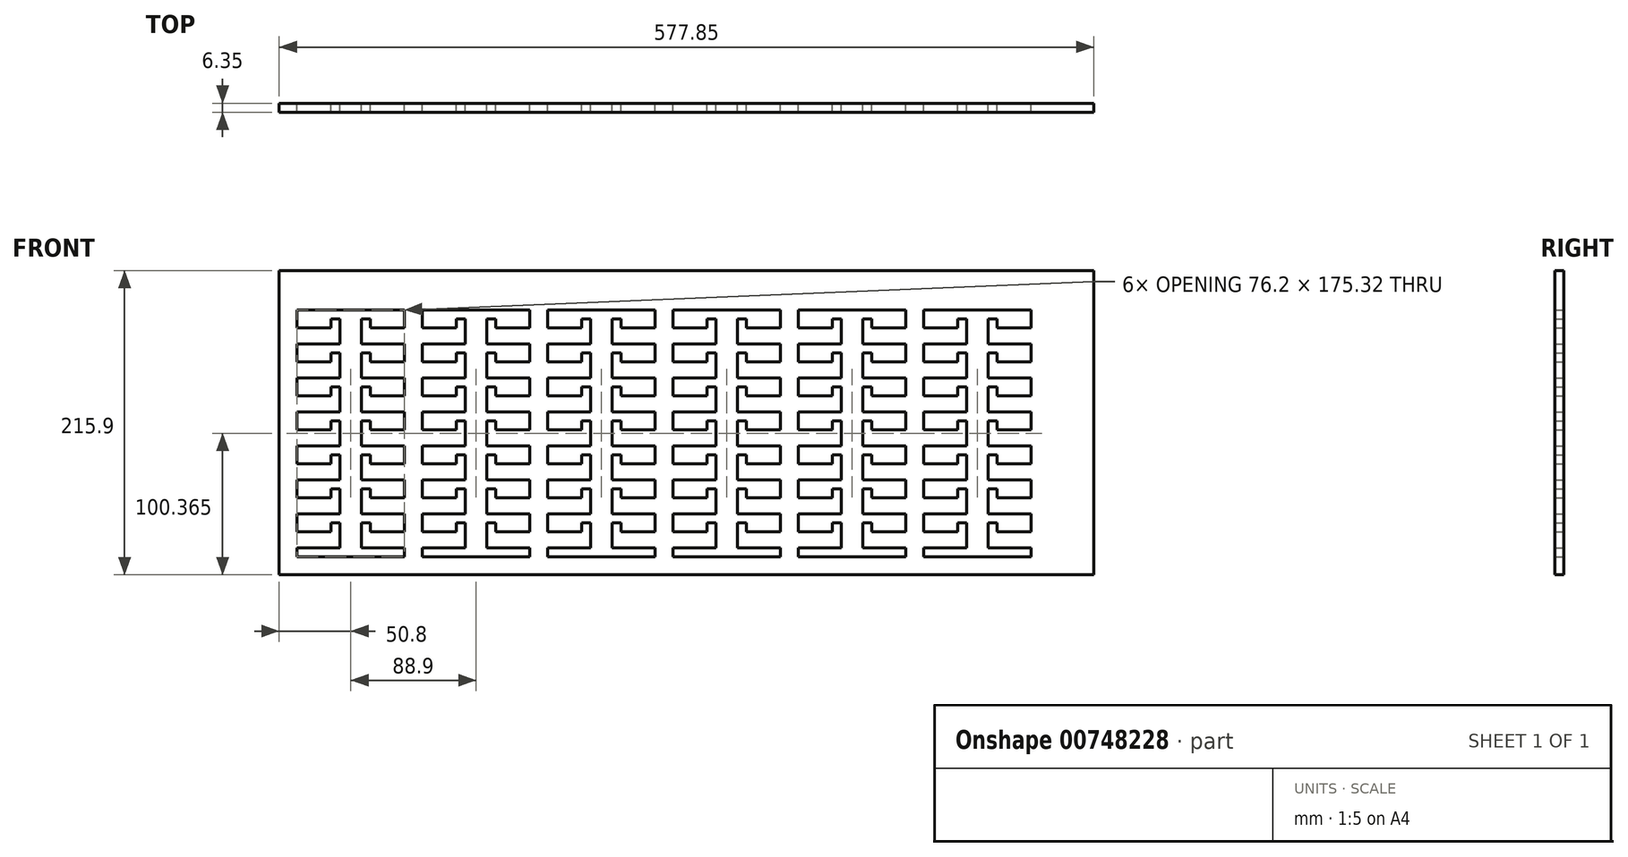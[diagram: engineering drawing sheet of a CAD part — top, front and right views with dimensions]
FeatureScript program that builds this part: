
annotation { "Feature Type Name" : "Feature", "Feature Type Description" : "" }
export const myFeature = defineFeature(function(context is Context, id is Id, definition is map)
    precondition{}
    {
        {
            var Q0;
            Q0=qCreatedBy(makeId("Front.planeOp"),FACE);
            var sketch = newSketch(context, id + "F0", { "sketchPlane" : qUnion([Q0])});
            skLineSegment(sketch, "E0", {"start": v(-97.96, -49.5) * mm, "end": v(-67.48, -49.5) * mm});
            skLineSegment(sketch, "E1", {"start": v(-67.48, -49.5) * mm, "end": v(-67.48, -31.72) * mm});
            skLineSegment(sketch, "E2", {"start": v(-67.48, -31.72) * mm, "end": v(-73.83, -31.72) * mm});
            skLineSegment(sketch, "E3", {"start": v(-73.83, -31.72) * mm, "end": v(-73.83, -38.07) * mm});
            skLineSegment(sketch, "E4", {"start": v(-73.83, -38.07) * mm, "end": v(-97.96, -38.07) * mm});
            skLineSegment(sketch, "E5", {"start": v(-97.96, -38.07) * mm, "end": v(-97.96, -25.37) * mm});
            skLineSegment(sketch, "E6", {"start": v(-97.96, -25.37) * mm, "end": v(-67.48, -25.37) * mm});
            skLineSegment(sketch, "E7", {"start": v(-67.48, -25.37) * mm, "end": v(-67.48, -7.6) * mm});
            skLineSegment(sketch, "E8", {"start": v(-67.48, -7.6) * mm, "end": v(-73.83, -7.6) * mm});
            skLineSegment(sketch, "E9", {"start": v(-73.83, -7.6) * mm, "end": v(-73.83, -13.94) * mm});
            skLineSegment(sketch, "E10", {"start": v(-73.83, -13.94) * mm, "end": v(-97.96, -13.94) * mm});
            skLineSegment(sketch, "E11", {"start": v(-97.96, -13.94) * mm, "end": v(-97.96, -1.24) * mm});
            skLineSegment(sketch, "E12", {"start": v(-97.96, -1.24) * mm, "end": v(-67.48, -1.24) * mm});
            skLineSegment(sketch, "E13", {"start": v(-67.48, -1.24) * mm, "end": v(-67.48, 16.54) * mm});
            skLineSegment(sketch, "E14", {"start": v(-67.48, 16.54) * mm, "end": v(-73.83, 16.54) * mm});
            skLineSegment(sketch, "E15", {"start": v(-73.83, 16.54) * mm, "end": v(-73.83, 10.19) * mm});
            skLineSegment(sketch, "E16", {"start": v(-73.83, 10.19) * mm, "end": v(-97.96, 10.19) * mm});
            skLineSegment(sketch, "E17", {"start": v(-97.96, 10.19) * mm, "end": v(-97.96, 22.89) * mm});
            skLineSegment(sketch, "E18", {"start": v(-97.96, 22.89) * mm, "end": v(-67.48, 22.89) * mm});
            skLineSegment(sketch, "E19", {"start": v(-67.48, 22.89) * mm, "end": v(-67.48, 40.67) * mm});
            skLineSegment(sketch, "E20", {"start": v(-67.48, 40.67) * mm, "end": v(-73.83, 40.67) * mm});
            skLineSegment(sketch, "E21", {"start": v(-73.83, 40.67) * mm, "end": v(-73.83, 34.32) * mm});
            skLineSegment(sketch, "E22", {"start": v(-73.83, 34.32) * mm, "end": v(-97.96, 34.32) * mm});
            skLineSegment(sketch, "E23", {"start": v(-97.96, 34.32) * mm, "end": v(-97.96, 47.02) * mm});
            skLineSegment(sketch, "E24", {"start": v(-21.76, -80.05) * mm, "end": v(-21.76, -73.63) * mm});
            skLineSegment(sketch, "E25", {"start": v(-21.76, -73.63) * mm, "end": v(-52.24, -73.63) * mm});
            skLineSegment(sketch, "E26", {"start": v(-52.24, -73.63) * mm, "end": v(-52.24, -55.85) * mm});
            skLineSegment(sketch, "E27", {"start": v(-52.24, -55.85) * mm, "end": v(-45.89, -55.85) * mm});
            skLineSegment(sketch, "E28", {"start": v(-45.89, -55.85) * mm, "end": v(-45.89, -62.2) * mm});
            skLineSegment(sketch, "E29", {"start": v(-45.89, -62.2) * mm, "end": v(-21.76, -62.2) * mm});
            skLineSegment(sketch, "E30", {"start": v(-21.76, -62.2) * mm, "end": v(-21.76, -49.5) * mm});
            skLineSegment(sketch, "E31", {"start": v(-21.76, -49.5) * mm, "end": v(-52.24, -49.5) * mm});
            skLineSegment(sketch, "E32", {"start": v(-52.24, -49.5) * mm, "end": v(-52.24, -31.72) * mm});
            skLineSegment(sketch, "E33", {"start": v(-52.24, -31.72) * mm, "end": v(-45.89, -31.72) * mm});
            skLineSegment(sketch, "E34", {"start": v(-45.89, -31.72) * mm, "end": v(-45.89, -38.07) * mm});
            skLineSegment(sketch, "E35", {"start": v(-45.89, -38.07) * mm, "end": v(-21.76, -38.07) * mm});
            skLineSegment(sketch, "E36", {"start": v(-21.76, -38.07) * mm, "end": v(-21.76, -25.37) * mm});
            skLineSegment(sketch, "E37", {"start": v(-21.76, -25.37) * mm, "end": v(-52.24, -25.37) * mm});
            skLineSegment(sketch, "E38", {"start": v(-52.24, -25.37) * mm, "end": v(-52.24, -7.6) * mm});
            skLineSegment(sketch, "E39", {"start": v(-52.24, -7.6) * mm, "end": v(-45.89, -7.6) * mm});
            skLineSegment(sketch, "E40", {"start": v(-45.89, -7.6) * mm, "end": v(-45.89, -13.94) * mm});
            skLineSegment(sketch, "E41", {"start": v(-45.89, -13.94) * mm, "end": v(-21.76, -13.94) * mm});
            skLineSegment(sketch, "E42", {"start": v(-21.76, -13.94) * mm, "end": v(-21.76, -1.24) * mm});
            skLineSegment(sketch, "E43", {"start": v(-21.76, -1.24) * mm, "end": v(-52.24, -1.24) * mm});
            skLineSegment(sketch, "E44", {"start": v(-52.24, -1.24) * mm, "end": v(-52.24, 16.54) * mm});
            skLineSegment(sketch, "E45", {"start": v(-52.24, 16.54) * mm, "end": v(-45.89, 16.54) * mm});
            skLineSegment(sketch, "E46", {"start": v(-45.89, 16.54) * mm, "end": v(-45.89, 10.19) * mm});
            skLineSegment(sketch, "E47", {"start": v(-45.89, 10.19) * mm, "end": v(-21.76, 10.19) * mm});
            skLineSegment(sketch, "E48", {"start": v(-21.76, 10.19) * mm, "end": v(-21.76, 22.89) * mm});
            skLineSegment(sketch, "E49", {"start": v(-21.76, 22.89) * mm, "end": v(-52.24, 22.89) * mm});
            skLineSegment(sketch, "E50", {"start": v(-52.24, 22.89) * mm, "end": v(-52.24, 40.67) * mm});
            skLineSegment(sketch, "E51", {"start": v(-52.24, 40.67) * mm, "end": v(-45.89, 40.67) * mm});
            skLineSegment(sketch, "E52", {"start": v(-45.89, 40.67) * mm, "end": v(-45.89, 34.32) * mm});
            skLineSegment(sketch, "E53", {"start": v(-45.89, 34.32) * mm, "end": v(-21.76, 34.32) * mm});
            skLineSegment(sketch, "E54", {"start": v(-21.76, 34.32) * mm, "end": v(-21.76, 47.02) * mm});
            skLineSegment(sketch, "E55", {"start": v(-67.48, -73.63) * mm, "end": v(-67.48, -55.85) * mm});
            skLineSegment(sketch, "E56", {"start": v(-73.83, -62.2) * mm, "end": v(-73.83, -55.85) * mm});
            skLineSegment(sketch, "E57", {"start": v(-73.83, -55.85) * mm, "end": v(-67.48, -55.85) * mm});
            skLineSegment(sketch, "E58", {"start": v(-67.48, -73.63) * mm, "end": v(-97.96, -73.63) * mm});
            skLineSegment(sketch, "E59", {"start": v(-97.96, -62.2) * mm, "end": v(-97.96, -49.5) * mm});
            skLineSegment(sketch, "E60", {"start": v(-97.96, -73.63) * mm, "end": v(-97.96, -80.05) * mm});
            skLineSegment(sketch, "E61", {"start": v(-97.96, -62.2) * mm, "end": v(-73.83, -62.2) * mm});
            skLineSegment(sketch, "E62", {"start": v(-97.96, -80.05) * mm, "end": v(-21.76, -80.05) * mm});
            skPoint(sketch, "E63", {"position": v(-59.86, -80.05) * mm});
            skLineSegment(sketch, "E64", {"start": v(-186.86, -49.5) * mm, "end": v(-156.38, -49.5) * mm});
            skLineSegment(sketch, "E65", {"start": v(-156.38, -49.5) * mm, "end": v(-156.38, -31.72) * mm});
            skLineSegment(sketch, "E66", {"start": v(-156.38, -31.72) * mm, "end": v(-162.73, -31.72) * mm});
            skLineSegment(sketch, "E67", {"start": v(-162.73, -31.72) * mm, "end": v(-162.73, -38.07) * mm});
            skLineSegment(sketch, "E68", {"start": v(-162.73, -38.07) * mm, "end": v(-186.86, -38.07) * mm});
            skLineSegment(sketch, "E69", {"start": v(-186.86, -38.07) * mm, "end": v(-186.86, -25.37) * mm});
            skLineSegment(sketch, "E70", {"start": v(-186.86, -25.37) * mm, "end": v(-156.38, -25.37) * mm});
            skLineSegment(sketch, "E71", {"start": v(-156.38, -25.37) * mm, "end": v(-156.38, -7.6) * mm});
            skLineSegment(sketch, "E72", {"start": v(-156.38, -7.6) * mm, "end": v(-162.73, -7.6) * mm});
            skLineSegment(sketch, "E73", {"start": v(-162.73, -7.6) * mm, "end": v(-162.73, -13.94) * mm});
            skLineSegment(sketch, "E74", {"start": v(-162.73, -13.94) * mm, "end": v(-186.86, -13.94) * mm});
            skLineSegment(sketch, "E75", {"start": v(-186.86, -13.94) * mm, "end": v(-186.86, -1.24) * mm});
            skLineSegment(sketch, "E76", {"start": v(-186.86, -1.24) * mm, "end": v(-156.38, -1.24) * mm});
            skLineSegment(sketch, "E77", {"start": v(-156.38, -1.24) * mm, "end": v(-156.38, 16.54) * mm});
            skLineSegment(sketch, "E78", {"start": v(-156.38, 16.54) * mm, "end": v(-162.73, 16.54) * mm});
            skLineSegment(sketch, "E79", {"start": v(-162.73, 16.54) * mm, "end": v(-162.73, 10.19) * mm});
            skLineSegment(sketch, "E80", {"start": v(-162.73, 10.19) * mm, "end": v(-186.86, 10.19) * mm});
            skLineSegment(sketch, "E81", {"start": v(-186.86, 10.19) * mm, "end": v(-186.86, 22.89) * mm});
            skLineSegment(sketch, "E82", {"start": v(-186.86, 22.89) * mm, "end": v(-156.38, 22.89) * mm});
            skLineSegment(sketch, "E83", {"start": v(-156.38, 22.89) * mm, "end": v(-156.38, 40.67) * mm});
            skLineSegment(sketch, "E84", {"start": v(-156.38, 40.67) * mm, "end": v(-162.73, 40.67) * mm});
            skLineSegment(sketch, "E85", {"start": v(-162.73, 40.67) * mm, "end": v(-162.73, 34.32) * mm});
            skLineSegment(sketch, "E86", {"start": v(-162.73, 34.32) * mm, "end": v(-186.86, 34.32) * mm});
            skLineSegment(sketch, "E87", {"start": v(-186.86, 34.32) * mm, "end": v(-186.86, 47.02) * mm});
            skLineSegment(sketch, "E88", {"start": v(-110.66, -80.05) * mm, "end": v(-110.66, -73.63) * mm});
            skLineSegment(sketch, "E89", {"start": v(-110.66, -73.63) * mm, "end": v(-141.14, -73.63) * mm});
            skLineSegment(sketch, "E90", {"start": v(-141.14, -73.63) * mm, "end": v(-141.14, -55.85) * mm});
            skLineSegment(sketch, "E91", {"start": v(-141.14, -55.85) * mm, "end": v(-134.79, -55.85) * mm});
            skLineSegment(sketch, "E92", {"start": v(-134.79, -55.85) * mm, "end": v(-134.79, -62.2) * mm});
            skLineSegment(sketch, "E93", {"start": v(-134.79, -62.2) * mm, "end": v(-110.66, -62.2) * mm});
            skLineSegment(sketch, "E94", {"start": v(-110.66, -62.2) * mm, "end": v(-110.66, -49.5) * mm});
            skLineSegment(sketch, "E95", {"start": v(-110.66, -49.5) * mm, "end": v(-141.14, -49.5) * mm});
            skLineSegment(sketch, "E96", {"start": v(-141.14, -49.5) * mm, "end": v(-141.14, -31.72) * mm});
            skLineSegment(sketch, "E97", {"start": v(-141.14, -31.72) * mm, "end": v(-134.79, -31.72) * mm});
            skLineSegment(sketch, "E98", {"start": v(-134.79, -31.72) * mm, "end": v(-134.79, -38.07) * mm});
            skLineSegment(sketch, "E99", {"start": v(-134.79, -38.07) * mm, "end": v(-110.66, -38.07) * mm});
            skLineSegment(sketch, "E100", {"start": v(-110.66, -38.07) * mm, "end": v(-110.66, -25.37) * mm});
            skLineSegment(sketch, "E101", {"start": v(-110.66, -25.37) * mm, "end": v(-141.14, -25.37) * mm});
            skLineSegment(sketch, "E102", {"start": v(-141.14, -25.37) * mm, "end": v(-141.14, -7.6) * mm});
            skLineSegment(sketch, "E103", {"start": v(-141.14, -7.6) * mm, "end": v(-134.79, -7.6) * mm});
            skLineSegment(sketch, "E104", {"start": v(-134.79, -7.6) * mm, "end": v(-134.79, -13.94) * mm});
            skLineSegment(sketch, "E105", {"start": v(-134.79, -13.94) * mm, "end": v(-110.66, -13.94) * mm});
            skLineSegment(sketch, "E106", {"start": v(-110.66, -13.94) * mm, "end": v(-110.66, -1.24) * mm});
            skLineSegment(sketch, "E107", {"start": v(-110.66, -1.24) * mm, "end": v(-141.14, -1.24) * mm});
            skLineSegment(sketch, "E108", {"start": v(-141.14, -1.24) * mm, "end": v(-141.14, 16.54) * mm});
            skLineSegment(sketch, "E109", {"start": v(-141.14, 16.54) * mm, "end": v(-134.79, 16.54) * mm});
            skLineSegment(sketch, "E110", {"start": v(-134.79, 16.54) * mm, "end": v(-134.79, 10.19) * mm});
            skLineSegment(sketch, "E111", {"start": v(-134.79, 10.19) * mm, "end": v(-110.66, 10.19) * mm});
            skLineSegment(sketch, "E112", {"start": v(-110.66, 10.19) * mm, "end": v(-110.66, 22.89) * mm});
            skLineSegment(sketch, "E113", {"start": v(-110.66, 22.89) * mm, "end": v(-141.14, 22.89) * mm});
            skLineSegment(sketch, "E114", {"start": v(-141.14, 22.89) * mm, "end": v(-141.14, 40.67) * mm});
            skLineSegment(sketch, "E115", {"start": v(-141.14, 40.67) * mm, "end": v(-134.79, 40.67) * mm});
            skLineSegment(sketch, "E116", {"start": v(-134.79, 40.67) * mm, "end": v(-134.79, 34.32) * mm});
            skLineSegment(sketch, "E117", {"start": v(-134.79, 34.32) * mm, "end": v(-110.66, 34.32) * mm});
            skLineSegment(sketch, "E118", {"start": v(-110.66, 34.32) * mm, "end": v(-110.66, 47.02) * mm});
            skLineSegment(sketch, "E119", {"start": v(-156.38, -73.63) * mm, "end": v(-156.38, -55.85) * mm});
            skLineSegment(sketch, "E120", {"start": v(-162.73, -62.2) * mm, "end": v(-162.73, -55.85) * mm});
            skLineSegment(sketch, "E121", {"start": v(-162.73, -55.85) * mm, "end": v(-156.38, -55.85) * mm});
            skLineSegment(sketch, "E122", {"start": v(-156.38, -73.63) * mm, "end": v(-186.86, -73.63) * mm});
            skLineSegment(sketch, "E123", {"start": v(-186.86, -62.2) * mm, "end": v(-186.86, -49.5) * mm});
            skLineSegment(sketch, "E124", {"start": v(-186.86, -73.63) * mm, "end": v(-186.86, -80.05) * mm});
            skLineSegment(sketch, "E125", {"start": v(-186.86, -62.2) * mm, "end": v(-162.73, -62.2) * mm});
            skLineSegment(sketch, "E126", {"start": v(-186.86, -80.05) * mm, "end": v(-110.66, -80.05) * mm});
            skPoint(sketch, "E127", {"position": v(-148.76, -80.05) * mm});
            skLineSegment(sketch, "E128", {"start": v(-275.76, -49.5) * mm, "end": v(-245.28, -49.5) * mm});
            skLineSegment(sketch, "E129", {"start": v(-245.28, -49.5) * mm, "end": v(-245.28, -31.72) * mm});
            skLineSegment(sketch, "E130", {"start": v(-245.28, -31.72) * mm, "end": v(-251.63, -31.72) * mm});
            skLineSegment(sketch, "E131", {"start": v(-251.63, -31.72) * mm, "end": v(-251.63, -38.07) * mm});
            skLineSegment(sketch, "E132", {"start": v(-251.63, -38.07) * mm, "end": v(-275.76, -38.07) * mm});
            skLineSegment(sketch, "E133", {"start": v(-275.76, -38.07) * mm, "end": v(-275.76, -25.37) * mm});
            skLineSegment(sketch, "E134", {"start": v(-275.76, -25.37) * mm, "end": v(-245.28, -25.37) * mm});
            skLineSegment(sketch, "E135", {"start": v(-245.28, -25.37) * mm, "end": v(-245.28, -7.6) * mm});
            skLineSegment(sketch, "E136", {"start": v(-245.28, -7.6) * mm, "end": v(-251.63, -7.6) * mm});
            skLineSegment(sketch, "E137", {"start": v(-251.63, -7.6) * mm, "end": v(-251.63, -13.94) * mm});
            skLineSegment(sketch, "E138", {"start": v(-251.63, -13.94) * mm, "end": v(-275.76, -13.94) * mm});
            skLineSegment(sketch, "E139", {"start": v(-275.76, -13.94) * mm, "end": v(-275.76, -1.24) * mm});
            skLineSegment(sketch, "E140", {"start": v(-275.76, -1.24) * mm, "end": v(-245.28, -1.24) * mm});
            skLineSegment(sketch, "E141", {"start": v(-245.28, -1.24) * mm, "end": v(-245.28, 16.54) * mm});
            skLineSegment(sketch, "E142", {"start": v(-245.28, 16.54) * mm, "end": v(-251.63, 16.54) * mm});
            skLineSegment(sketch, "E143", {"start": v(-251.63, 16.54) * mm, "end": v(-251.63, 10.19) * mm});
            skLineSegment(sketch, "E144", {"start": v(-251.63, 10.19) * mm, "end": v(-275.76, 10.19) * mm});
            skLineSegment(sketch, "E145", {"start": v(-275.76, 10.19) * mm, "end": v(-275.76, 22.89) * mm});
            skLineSegment(sketch, "E146", {"start": v(-275.76, 22.89) * mm, "end": v(-245.28, 22.89) * mm});
            skLineSegment(sketch, "E147", {"start": v(-245.28, 22.89) * mm, "end": v(-245.28, 40.67) * mm});
            skLineSegment(sketch, "E148", {"start": v(-245.28, 40.67) * mm, "end": v(-251.63, 40.67) * mm});
            skLineSegment(sketch, "E149", {"start": v(-251.63, 40.67) * mm, "end": v(-251.63, 34.32) * mm});
            skLineSegment(sketch, "E150", {"start": v(-251.63, 34.32) * mm, "end": v(-275.76, 34.32) * mm});
            skLineSegment(sketch, "E151", {"start": v(-275.76, 34.32) * mm, "end": v(-275.76, 47.02) * mm});
            skLineSegment(sketch, "E152", {"start": v(-199.56, -80.05) * mm, "end": v(-199.56, -73.63) * mm});
            skLineSegment(sketch, "E153", {"start": v(-199.56, -73.63) * mm, "end": v(-230.04, -73.63) * mm});
            skLineSegment(sketch, "E154", {"start": v(-230.04, -73.63) * mm, "end": v(-230.04, -55.85) * mm});
            skLineSegment(sketch, "E155", {"start": v(-230.04, -55.85) * mm, "end": v(-223.69, -55.85) * mm});
            skLineSegment(sketch, "E156", {"start": v(-223.69, -55.85) * mm, "end": v(-223.69, -62.2) * mm});
            skLineSegment(sketch, "E157", {"start": v(-223.69, -62.2) * mm, "end": v(-199.56, -62.2) * mm});
            skLineSegment(sketch, "E158", {"start": v(-199.56, -62.2) * mm, "end": v(-199.56, -49.5) * mm});
            skLineSegment(sketch, "E159", {"start": v(-199.56, -49.5) * mm, "end": v(-230.04, -49.5) * mm});
            skLineSegment(sketch, "E160", {"start": v(-230.04, -49.5) * mm, "end": v(-230.04, -31.72) * mm});
            skLineSegment(sketch, "E161", {"start": v(-230.04, -31.72) * mm, "end": v(-223.69, -31.72) * mm});
            skLineSegment(sketch, "E162", {"start": v(-223.69, -31.72) * mm, "end": v(-223.69, -38.07) * mm});
            skLineSegment(sketch, "E163", {"start": v(-223.69, -38.07) * mm, "end": v(-199.56, -38.07) * mm});
            skLineSegment(sketch, "E164", {"start": v(-199.56, -38.07) * mm, "end": v(-199.56, -25.37) * mm});
            skLineSegment(sketch, "E165", {"start": v(-199.56, -25.37) * mm, "end": v(-230.04, -25.37) * mm});
            skLineSegment(sketch, "E166", {"start": v(-230.04, -25.37) * mm, "end": v(-230.04, -7.6) * mm});
            skLineSegment(sketch, "E167", {"start": v(-230.04, -7.6) * mm, "end": v(-223.69, -7.6) * mm});
            skLineSegment(sketch, "E168", {"start": v(-223.69, -7.6) * mm, "end": v(-223.69, -13.94) * mm});
            skLineSegment(sketch, "E169", {"start": v(-223.69, -13.94) * mm, "end": v(-199.56, -13.94) * mm});
            skLineSegment(sketch, "E170", {"start": v(-199.56, -13.94) * mm, "end": v(-199.56, -1.24) * mm});
            skLineSegment(sketch, "E171", {"start": v(-199.56, -1.24) * mm, "end": v(-230.04, -1.24) * mm});
            skLineSegment(sketch, "E172", {"start": v(-230.04, -1.24) * mm, "end": v(-230.04, 16.54) * mm});
            skLineSegment(sketch, "E173", {"start": v(-230.04, 16.54) * mm, "end": v(-223.69, 16.54) * mm});
            skLineSegment(sketch, "E174", {"start": v(-223.69, 16.54) * mm, "end": v(-223.69, 10.19) * mm});
            skLineSegment(sketch, "E175", {"start": v(-223.69, 10.19) * mm, "end": v(-199.56, 10.19) * mm});
            skLineSegment(sketch, "E176", {"start": v(-199.56, 10.19) * mm, "end": v(-199.56, 22.89) * mm});
            skLineSegment(sketch, "E177", {"start": v(-199.56, 22.89) * mm, "end": v(-230.04, 22.89) * mm});
            skLineSegment(sketch, "E178", {"start": v(-230.04, 22.89) * mm, "end": v(-230.04, 40.67) * mm});
            skLineSegment(sketch, "E179", {"start": v(-230.04, 40.67) * mm, "end": v(-223.69, 40.67) * mm});
            skLineSegment(sketch, "E180", {"start": v(-223.69, 40.67) * mm, "end": v(-223.69, 34.32) * mm});
            skLineSegment(sketch, "E181", {"start": v(-223.69, 34.32) * mm, "end": v(-199.56, 34.32) * mm});
            skLineSegment(sketch, "E182", {"start": v(-199.56, 34.32) * mm, "end": v(-199.56, 47.02) * mm});
            skLineSegment(sketch, "E183", {"start": v(-245.28, -73.63) * mm, "end": v(-245.28, -55.85) * mm});
            skLineSegment(sketch, "E184", {"start": v(-251.63, -62.2) * mm, "end": v(-251.63, -55.85) * mm});
            skLineSegment(sketch, "E185", {"start": v(-251.63, -55.85) * mm, "end": v(-245.28, -55.85) * mm});
            skLineSegment(sketch, "E186", {"start": v(-245.28, -73.63) * mm, "end": v(-275.76, -73.63) * mm});
            skLineSegment(sketch, "E187", {"start": v(-275.76, -62.2) * mm, "end": v(-275.76, -49.5) * mm});
            skLineSegment(sketch, "E188", {"start": v(-275.76, -73.63) * mm, "end": v(-275.76, -80.05) * mm});
            skLineSegment(sketch, "E189", {"start": v(-275.76, -62.2) * mm, "end": v(-251.63, -62.2) * mm});
            skLineSegment(sketch, "E190", {"start": v(-275.76, -80.05) * mm, "end": v(-199.56, -80.05) * mm});
            skPoint(sketch, "E191", {"position": v(-237.66, -80.05) * mm});
            skLineSegment(sketch, "E192", {"start": v(-364.66, -49.5) * mm, "end": v(-334.18, -49.5) * mm});
            skLineSegment(sketch, "E193", {"start": v(-334.18, -49.5) * mm, "end": v(-334.18, -31.72) * mm});
            skLineSegment(sketch, "E194", {"start": v(-334.18, -31.72) * mm, "end": v(-340.53, -31.72) * mm});
            skLineSegment(sketch, "E195", {"start": v(-340.53, -31.72) * mm, "end": v(-340.53, -38.07) * mm});
            skLineSegment(sketch, "E196", {"start": v(-340.53, -38.07) * mm, "end": v(-364.66, -38.07) * mm});
            skLineSegment(sketch, "E197", {"start": v(-364.66, -38.07) * mm, "end": v(-364.66, -25.37) * mm});
            skLineSegment(sketch, "E198", {"start": v(-364.66, -25.37) * mm, "end": v(-334.18, -25.37) * mm});
            skLineSegment(sketch, "E199", {"start": v(-334.18, -25.37) * mm, "end": v(-334.18, -7.6) * mm});
            skLineSegment(sketch, "E200", {"start": v(-334.18, -7.6) * mm, "end": v(-340.53, -7.6) * mm});
            skLineSegment(sketch, "E201", {"start": v(-340.53, -7.6) * mm, "end": v(-340.53, -13.94) * mm});
            skLineSegment(sketch, "E202", {"start": v(-340.53, -13.94) * mm, "end": v(-364.66, -13.94) * mm});
            skLineSegment(sketch, "E203", {"start": v(-364.66, -13.94) * mm, "end": v(-364.66, -1.24) * mm});
            skLineSegment(sketch, "E204", {"start": v(-364.66, -1.24) * mm, "end": v(-334.18, -1.24) * mm});
            skLineSegment(sketch, "E205", {"start": v(-334.18, -1.24) * mm, "end": v(-334.18, 16.54) * mm});
            skLineSegment(sketch, "E206", {"start": v(-334.18, 16.54) * mm, "end": v(-340.53, 16.54) * mm});
            skLineSegment(sketch, "E207", {"start": v(-340.53, 16.54) * mm, "end": v(-340.53, 10.19) * mm});
            skLineSegment(sketch, "E208", {"start": v(-340.53, 10.19) * mm, "end": v(-364.66, 10.19) * mm});
            skLineSegment(sketch, "E209", {"start": v(-364.66, 10.19) * mm, "end": v(-364.66, 22.89) * mm});
            skLineSegment(sketch, "E210", {"start": v(-364.66, 22.89) * mm, "end": v(-334.18, 22.89) * mm});
            skLineSegment(sketch, "E211", {"start": v(-334.18, 22.89) * mm, "end": v(-334.18, 40.67) * mm});
            skLineSegment(sketch, "E212", {"start": v(-334.18, 40.67) * mm, "end": v(-340.53, 40.67) * mm});
            skLineSegment(sketch, "E213", {"start": v(-340.53, 40.67) * mm, "end": v(-340.53, 34.32) * mm});
            skLineSegment(sketch, "E214", {"start": v(-340.53, 34.32) * mm, "end": v(-364.66, 34.32) * mm});
            skLineSegment(sketch, "E215", {"start": v(-364.66, 34.32) * mm, "end": v(-364.66, 47.02) * mm});
            skLineSegment(sketch, "E216", {"start": v(-288.46, -80.05) * mm, "end": v(-288.46, -73.63) * mm});
            skLineSegment(sketch, "E217", {"start": v(-288.46, -73.63) * mm, "end": v(-318.94, -73.63) * mm});
            skLineSegment(sketch, "E218", {"start": v(-318.94, -73.63) * mm, "end": v(-318.94, -55.85) * mm});
            skLineSegment(sketch, "E219", {"start": v(-318.94, -55.85) * mm, "end": v(-312.59, -55.85) * mm});
            skLineSegment(sketch, "E220", {"start": v(-312.59, -55.85) * mm, "end": v(-312.59, -62.2) * mm});
            skLineSegment(sketch, "E221", {"start": v(-312.59, -62.2) * mm, "end": v(-288.46, -62.2) * mm});
            skLineSegment(sketch, "E222", {"start": v(-288.46, -62.2) * mm, "end": v(-288.46, -49.5) * mm});
            skLineSegment(sketch, "E223", {"start": v(-288.46, -49.5) * mm, "end": v(-318.94, -49.5) * mm});
            skLineSegment(sketch, "E224", {"start": v(-318.94, -49.5) * mm, "end": v(-318.94, -31.72) * mm});
            skLineSegment(sketch, "E225", {"start": v(-318.94, -31.72) * mm, "end": v(-312.59, -31.72) * mm});
            skLineSegment(sketch, "E226", {"start": v(-312.59, -31.72) * mm, "end": v(-312.59, -38.07) * mm});
            skLineSegment(sketch, "E227", {"start": v(-312.59, -38.07) * mm, "end": v(-288.46, -38.07) * mm});
            skLineSegment(sketch, "E228", {"start": v(-288.46, -38.07) * mm, "end": v(-288.46, -25.37) * mm});
            skLineSegment(sketch, "E229", {"start": v(-288.46, -25.37) * mm, "end": v(-318.94, -25.37) * mm});
            skLineSegment(sketch, "E230", {"start": v(-318.94, -25.37) * mm, "end": v(-318.94, -7.6) * mm});
            skLineSegment(sketch, "E231", {"start": v(-318.94, -7.6) * mm, "end": v(-312.59, -7.6) * mm});
            skLineSegment(sketch, "E232", {"start": v(-312.59, -7.6) * mm, "end": v(-312.59, -13.94) * mm});
            skLineSegment(sketch, "E233", {"start": v(-312.59, -13.94) * mm, "end": v(-288.46, -13.94) * mm});
            skLineSegment(sketch, "E234", {"start": v(-288.46, -13.94) * mm, "end": v(-288.46, -1.24) * mm});
            skLineSegment(sketch, "E235", {"start": v(-288.46, -1.24) * mm, "end": v(-318.94, -1.24) * mm});
            skLineSegment(sketch, "E236", {"start": v(-318.94, -1.24) * mm, "end": v(-318.94, 16.54) * mm});
            skLineSegment(sketch, "E237", {"start": v(-318.94, 16.54) * mm, "end": v(-312.59, 16.54) * mm});
            skLineSegment(sketch, "E238", {"start": v(-312.59, 16.54) * mm, "end": v(-312.59, 10.19) * mm});
            skLineSegment(sketch, "E239", {"start": v(-312.59, 10.19) * mm, "end": v(-288.46, 10.19) * mm});
            skLineSegment(sketch, "E240", {"start": v(-288.46, 10.19) * mm, "end": v(-288.46, 22.89) * mm});
            skLineSegment(sketch, "E241", {"start": v(-288.46, 22.89) * mm, "end": v(-318.94, 22.89) * mm});
            skLineSegment(sketch, "E242", {"start": v(-318.94, 22.89) * mm, "end": v(-318.94, 40.67) * mm});
            skLineSegment(sketch, "E243", {"start": v(-318.94, 40.67) * mm, "end": v(-312.59, 40.67) * mm});
            skLineSegment(sketch, "E244", {"start": v(-312.59, 40.67) * mm, "end": v(-312.59, 34.32) * mm});
            skLineSegment(sketch, "E245", {"start": v(-312.59, 34.32) * mm, "end": v(-288.46, 34.32) * mm});
            skLineSegment(sketch, "E246", {"start": v(-288.46, 34.32) * mm, "end": v(-288.46, 47.02) * mm});
            skLineSegment(sketch, "E247", {"start": v(-334.18, -73.63) * mm, "end": v(-334.18, -55.85) * mm});
            skLineSegment(sketch, "E248", {"start": v(-340.53, -62.2) * mm, "end": v(-340.53, -55.85) * mm});
            skLineSegment(sketch, "E249", {"start": v(-340.53, -55.85) * mm, "end": v(-334.18, -55.85) * mm});
            skLineSegment(sketch, "E250", {"start": v(-334.18, -73.63) * mm, "end": v(-364.66, -73.63) * mm});
            skLineSegment(sketch, "E251", {"start": v(-364.66, -62.2) * mm, "end": v(-364.66, -49.5) * mm});
            skLineSegment(sketch, "E252", {"start": v(-364.66, -73.63) * mm, "end": v(-364.66, -80.05) * mm});
            skLineSegment(sketch, "E253", {"start": v(-364.66, -62.2) * mm, "end": v(-340.53, -62.2) * mm});
            skLineSegment(sketch, "E254", {"start": v(-364.66, -80.05) * mm, "end": v(-288.46, -80.05) * mm});
            skPoint(sketch, "E255", {"position": v(-326.56, -80.05) * mm});
            skLineSegment(sketch, "E256.bottom", {"start": v(22.7, 123.15) * mm, "end": v(-555.16, 123.15) * mm});
            skLineSegment(sketch, "E256.top", {"start": v(22.7, -92.75) * mm, "end": v(-555.16, -92.75) * mm});
            skLineSegment(sketch, "E256.left", {"start": v(22.7, 123.15) * mm, "end": v(22.7, -92.75) * mm});
            skLineSegment(sketch, "E256.right", {"start": v(-555.16, 123.15) * mm, "end": v(-555.16, -92.75) * mm});
            skPoint(sketch, "E257", {"position": v(-266.23, 123.15) * mm});
            skLineSegment(sketch, "E258", {"start": v(-453.56, -49.5) * mm, "end": v(-423.08, -49.5) * mm});
            skLineSegment(sketch, "E259", {"start": v(-423.08, -49.5) * mm, "end": v(-423.08, -31.72) * mm});
            skLineSegment(sketch, "E260", {"start": v(-423.08, -31.72) * mm, "end": v(-429.43, -31.72) * mm});
            skLineSegment(sketch, "E261", {"start": v(-429.43, -31.72) * mm, "end": v(-429.43, -38.07) * mm});
            skLineSegment(sketch, "E262", {"start": v(-429.43, -38.07) * mm, "end": v(-453.56, -38.07) * mm});
            skLineSegment(sketch, "E263", {"start": v(-453.56, -38.07) * mm, "end": v(-453.56, -25.37) * mm});
            skLineSegment(sketch, "E264", {"start": v(-453.56, -25.37) * mm, "end": v(-423.08, -25.37) * mm});
            skLineSegment(sketch, "E265", {"start": v(-423.08, -25.37) * mm, "end": v(-423.08, -7.6) * mm});
            skLineSegment(sketch, "E266", {"start": v(-423.08, -7.6) * mm, "end": v(-429.43, -7.6) * mm});
            skLineSegment(sketch, "E267", {"start": v(-429.43, -7.6) * mm, "end": v(-429.43, -13.94) * mm});
            skLineSegment(sketch, "E268", {"start": v(-429.43, -13.94) * mm, "end": v(-453.56, -13.94) * mm});
            skLineSegment(sketch, "E269", {"start": v(-453.56, -13.94) * mm, "end": v(-453.56, -1.24) * mm});
            skLineSegment(sketch, "E270", {"start": v(-453.56, -1.24) * mm, "end": v(-423.08, -1.24) * mm});
            skLineSegment(sketch, "E271", {"start": v(-423.08, -1.24) * mm, "end": v(-423.08, 16.54) * mm});
            skLineSegment(sketch, "E272", {"start": v(-423.08, 16.54) * mm, "end": v(-429.43, 16.54) * mm});
            skLineSegment(sketch, "E273", {"start": v(-429.43, 16.54) * mm, "end": v(-429.43, 10.19) * mm});
            skLineSegment(sketch, "E274", {"start": v(-429.43, 10.19) * mm, "end": v(-453.56, 10.19) * mm});
            skLineSegment(sketch, "E275", {"start": v(-453.56, 10.19) * mm, "end": v(-453.56, 22.89) * mm});
            skLineSegment(sketch, "E276", {"start": v(-453.56, 22.89) * mm, "end": v(-423.08, 22.89) * mm});
            skLineSegment(sketch, "E277", {"start": v(-423.08, 22.89) * mm, "end": v(-423.08, 40.67) * mm});
            skLineSegment(sketch, "E278", {"start": v(-423.08, 40.67) * mm, "end": v(-429.43, 40.67) * mm});
            skLineSegment(sketch, "E279", {"start": v(-429.43, 40.67) * mm, "end": v(-429.43, 34.32) * mm});
            skLineSegment(sketch, "E280", {"start": v(-429.43, 34.32) * mm, "end": v(-453.56, 34.32) * mm});
            skLineSegment(sketch, "E281", {"start": v(-453.56, 34.32) * mm, "end": v(-453.56, 47.02) * mm});
            skLineSegment(sketch, "E282", {"start": v(-377.36, -80.05) * mm, "end": v(-377.36, -73.63) * mm});
            skLineSegment(sketch, "E283", {"start": v(-377.36, -73.63) * mm, "end": v(-407.84, -73.63) * mm});
            skLineSegment(sketch, "E284", {"start": v(-407.84, -73.63) * mm, "end": v(-407.84, -55.85) * mm});
            skLineSegment(sketch, "E285", {"start": v(-407.84, -55.85) * mm, "end": v(-401.49, -55.85) * mm});
            skLineSegment(sketch, "E286", {"start": v(-401.49, -55.85) * mm, "end": v(-401.49, -62.2) * mm});
            skLineSegment(sketch, "E287", {"start": v(-401.49, -62.2) * mm, "end": v(-377.36, -62.2) * mm});
            skLineSegment(sketch, "E288", {"start": v(-377.36, -62.2) * mm, "end": v(-377.36, -49.5) * mm});
            skLineSegment(sketch, "E289", {"start": v(-377.36, -49.5) * mm, "end": v(-407.84, -49.5) * mm});
            skLineSegment(sketch, "E290", {"start": v(-407.84, -49.5) * mm, "end": v(-407.84, -31.72) * mm});
            skLineSegment(sketch, "E291", {"start": v(-407.84, -31.72) * mm, "end": v(-401.49, -31.72) * mm});
            skLineSegment(sketch, "E292", {"start": v(-401.49, -31.72) * mm, "end": v(-401.49, -38.07) * mm});
            skLineSegment(sketch, "E293", {"start": v(-401.49, -38.07) * mm, "end": v(-377.36, -38.07) * mm});
            skLineSegment(sketch, "E294", {"start": v(-377.36, -38.07) * mm, "end": v(-377.36, -25.37) * mm});
            skLineSegment(sketch, "E295", {"start": v(-377.36, -25.37) * mm, "end": v(-407.84, -25.37) * mm});
            skLineSegment(sketch, "E296", {"start": v(-407.84, -25.37) * mm, "end": v(-407.84, -7.6) * mm});
            skLineSegment(sketch, "E297", {"start": v(-407.84, -7.6) * mm, "end": v(-401.49, -7.6) * mm});
            skLineSegment(sketch, "E298", {"start": v(-401.49, -7.6) * mm, "end": v(-401.49, -13.94) * mm});
            skLineSegment(sketch, "E299", {"start": v(-401.49, -13.94) * mm, "end": v(-377.36, -13.94) * mm});
            skLineSegment(sketch, "E300", {"start": v(-377.36, -13.94) * mm, "end": v(-377.36, -1.24) * mm});
            skLineSegment(sketch, "E301", {"start": v(-377.36, -1.24) * mm, "end": v(-407.84, -1.24) * mm});
            skLineSegment(sketch, "E302", {"start": v(-407.84, -1.24) * mm, "end": v(-407.84, 16.54) * mm});
            skLineSegment(sketch, "E303", {"start": v(-407.84, 16.54) * mm, "end": v(-401.49, 16.54) * mm});
            skLineSegment(sketch, "E304", {"start": v(-401.49, 16.54) * mm, "end": v(-401.49, 10.19) * mm});
            skLineSegment(sketch, "E305", {"start": v(-401.49, 10.19) * mm, "end": v(-377.36, 10.19) * mm});
            skLineSegment(sketch, "E306", {"start": v(-377.36, 10.19) * mm, "end": v(-377.36, 22.89) * mm});
            skLineSegment(sketch, "E307", {"start": v(-377.36, 22.89) * mm, "end": v(-407.84, 22.89) * mm});
            skLineSegment(sketch, "E308", {"start": v(-407.84, 22.89) * mm, "end": v(-407.84, 40.67) * mm});
            skLineSegment(sketch, "E309", {"start": v(-407.84, 40.67) * mm, "end": v(-401.49, 40.67) * mm});
            skLineSegment(sketch, "E310", {"start": v(-401.49, 40.67) * mm, "end": v(-401.49, 34.32) * mm});
            skLineSegment(sketch, "E311", {"start": v(-401.49, 34.32) * mm, "end": v(-377.36, 34.32) * mm});
            skLineSegment(sketch, "E312", {"start": v(-377.36, 34.32) * mm, "end": v(-377.36, 47.02) * mm});
            skLineSegment(sketch, "E313", {"start": v(-423.08, -73.63) * mm, "end": v(-423.08, -55.85) * mm});
            skLineSegment(sketch, "E314", {"start": v(-429.43, -62.2) * mm, "end": v(-429.43, -55.85) * mm});
            skLineSegment(sketch, "E315", {"start": v(-429.43, -55.85) * mm, "end": v(-423.08, -55.85) * mm});
            skLineSegment(sketch, "E316", {"start": v(-423.08, -73.63) * mm, "end": v(-453.56, -73.63) * mm});
            skLineSegment(sketch, "E317", {"start": v(-453.56, -62.2) * mm, "end": v(-453.56, -49.5) * mm});
            skLineSegment(sketch, "E318", {"start": v(-453.56, -73.63) * mm, "end": v(-453.56, -80.05) * mm});
            skLineSegment(sketch, "E319", {"start": v(-453.56, -62.2) * mm, "end": v(-429.43, -62.2) * mm});
            skLineSegment(sketch, "E320", {"start": v(-453.56, -80.05) * mm, "end": v(-377.36, -80.05) * mm});
            skPoint(sketch, "E321", {"position": v(-415.46, -80.05) * mm});
            skLineSegment(sketch, "E322", {"start": v(-542.46, -49.5) * mm, "end": v(-511.98, -49.5) * mm});
            skLineSegment(sketch, "E323", {"start": v(-511.98, -49.5) * mm, "end": v(-511.98, -31.72) * mm});
            skLineSegment(sketch, "E324", {"start": v(-511.98, -31.72) * mm, "end": v(-518.33, -31.72) * mm});
            skLineSegment(sketch, "E325", {"start": v(-518.33, -31.72) * mm, "end": v(-518.33, -38.07) * mm});
            skLineSegment(sketch, "E326", {"start": v(-518.33, -38.07) * mm, "end": v(-542.46, -38.07) * mm});
            skLineSegment(sketch, "E327", {"start": v(-542.46, -38.07) * mm, "end": v(-542.46, -25.37) * mm});
            skLineSegment(sketch, "E328", {"start": v(-542.46, -25.37) * mm, "end": v(-511.98, -25.37) * mm});
            skLineSegment(sketch, "E329", {"start": v(-511.98, -25.37) * mm, "end": v(-511.98, -7.6) * mm});
            skLineSegment(sketch, "E330", {"start": v(-511.98, -7.6) * mm, "end": v(-518.33, -7.6) * mm});
            skLineSegment(sketch, "E331", {"start": v(-518.33, -7.6) * mm, "end": v(-518.33, -13.94) * mm});
            skLineSegment(sketch, "E332", {"start": v(-518.33, -13.94) * mm, "end": v(-542.46, -13.94) * mm});
            skLineSegment(sketch, "E333", {"start": v(-542.46, -13.94) * mm, "end": v(-542.46, -1.24) * mm});
            skLineSegment(sketch, "E334", {"start": v(-542.46, -1.24) * mm, "end": v(-511.98, -1.24) * mm});
            skLineSegment(sketch, "E335", {"start": v(-511.98, -1.24) * mm, "end": v(-511.98, 16.54) * mm});
            skLineSegment(sketch, "E336", {"start": v(-511.98, 16.54) * mm, "end": v(-518.33, 16.54) * mm});
            skLineSegment(sketch, "E337", {"start": v(-518.33, 16.54) * mm, "end": v(-518.33, 10.19) * mm});
            skLineSegment(sketch, "E338", {"start": v(-518.33, 10.19) * mm, "end": v(-542.46, 10.19) * mm});
            skLineSegment(sketch, "E339", {"start": v(-542.46, 10.19) * mm, "end": v(-542.46, 22.89) * mm});
            skLineSegment(sketch, "E340", {"start": v(-542.46, 22.89) * mm, "end": v(-511.98, 22.89) * mm});
            skLineSegment(sketch, "E341", {"start": v(-511.98, 22.89) * mm, "end": v(-511.98, 40.67) * mm});
            skLineSegment(sketch, "E342", {"start": v(-511.98, 40.67) * mm, "end": v(-518.33, 40.67) * mm});
            skLineSegment(sketch, "E343", {"start": v(-518.33, 40.67) * mm, "end": v(-518.33, 34.32) * mm});
            skLineSegment(sketch, "E344", {"start": v(-518.33, 34.32) * mm, "end": v(-542.46, 34.32) * mm});
            skLineSegment(sketch, "E345", {"start": v(-542.46, 34.32) * mm, "end": v(-542.46, 47.02) * mm});
            skLineSegment(sketch, "E346", {"start": v(-466.26, -80.05) * mm, "end": v(-466.26, -73.63) * mm});
            skLineSegment(sketch, "E347", {"start": v(-466.26, -73.63) * mm, "end": v(-496.74, -73.63) * mm});
            skLineSegment(sketch, "E348", {"start": v(-496.74, -73.63) * mm, "end": v(-496.74, -55.85) * mm});
            skLineSegment(sketch, "E349", {"start": v(-496.74, -55.85) * mm, "end": v(-490.39, -55.85) * mm});
            skLineSegment(sketch, "E350", {"start": v(-490.39, -55.85) * mm, "end": v(-490.39, -62.2) * mm});
            skLineSegment(sketch, "E351", {"start": v(-490.39, -62.2) * mm, "end": v(-466.26, -62.2) * mm});
            skLineSegment(sketch, "E352", {"start": v(-466.26, -62.2) * mm, "end": v(-466.26, -49.5) * mm});
            skLineSegment(sketch, "E353", {"start": v(-466.26, -49.5) * mm, "end": v(-496.74, -49.5) * mm});
            skLineSegment(sketch, "E354", {"start": v(-496.74, -49.5) * mm, "end": v(-496.74, -31.72) * mm});
            skLineSegment(sketch, "E355", {"start": v(-496.74, -31.72) * mm, "end": v(-490.39, -31.72) * mm});
            skLineSegment(sketch, "E356", {"start": v(-490.39, -31.72) * mm, "end": v(-490.39, -38.07) * mm});
            skLineSegment(sketch, "E357", {"start": v(-490.39, -38.07) * mm, "end": v(-466.26, -38.07) * mm});
            skLineSegment(sketch, "E358", {"start": v(-466.26, -38.07) * mm, "end": v(-466.26, -25.37) * mm});
            skLineSegment(sketch, "E359", {"start": v(-466.26, -25.37) * mm, "end": v(-496.74, -25.37) * mm});
            skLineSegment(sketch, "E360", {"start": v(-496.74, -25.37) * mm, "end": v(-496.74, -7.6) * mm});
            skLineSegment(sketch, "E361", {"start": v(-496.74, -7.6) * mm, "end": v(-490.39, -7.6) * mm});
            skLineSegment(sketch, "E362", {"start": v(-490.39, -7.6) * mm, "end": v(-490.39, -13.94) * mm});
            skLineSegment(sketch, "E363", {"start": v(-490.39, -13.94) * mm, "end": v(-466.26, -13.94) * mm});
            skLineSegment(sketch, "E364", {"start": v(-466.26, -13.94) * mm, "end": v(-466.26, -1.24) * mm});
            skLineSegment(sketch, "E365", {"start": v(-466.26, -1.24) * mm, "end": v(-496.74, -1.24) * mm});
            skLineSegment(sketch, "E366", {"start": v(-496.74, -1.24) * mm, "end": v(-496.74, 16.54) * mm});
            skLineSegment(sketch, "E367", {"start": v(-496.74, 16.54) * mm, "end": v(-490.39, 16.54) * mm});
            skLineSegment(sketch, "E368", {"start": v(-490.39, 16.54) * mm, "end": v(-490.39, 10.19) * mm});
            skLineSegment(sketch, "E369", {"start": v(-490.39, 10.19) * mm, "end": v(-466.26, 10.19) * mm});
            skLineSegment(sketch, "E370", {"start": v(-466.26, 10.19) * mm, "end": v(-466.26, 22.89) * mm});
            skLineSegment(sketch, "E371", {"start": v(-466.26, 22.89) * mm, "end": v(-496.74, 22.89) * mm});
            skLineSegment(sketch, "E372", {"start": v(-496.74, 22.89) * mm, "end": v(-496.74, 40.67) * mm});
            skLineSegment(sketch, "E373", {"start": v(-496.74, 40.67) * mm, "end": v(-490.39, 40.67) * mm});
            skLineSegment(sketch, "E374", {"start": v(-490.39, 40.67) * mm, "end": v(-490.39, 34.32) * mm});
            skLineSegment(sketch, "E375", {"start": v(-490.39, 34.32) * mm, "end": v(-466.26, 34.32) * mm});
            skLineSegment(sketch, "E376", {"start": v(-466.26, 34.32) * mm, "end": v(-466.26, 47.02) * mm});
            skLineSegment(sketch, "E377", {"start": v(-511.98, -73.63) * mm, "end": v(-511.98, -55.85) * mm});
            skLineSegment(sketch, "E378", {"start": v(-518.33, -62.2) * mm, "end": v(-518.33, -55.85) * mm});
            skLineSegment(sketch, "E379", {"start": v(-518.33, -55.85) * mm, "end": v(-511.98, -55.85) * mm});
            skLineSegment(sketch, "E380", {"start": v(-511.98, -73.63) * mm, "end": v(-542.46, -73.63) * mm});
            skLineSegment(sketch, "E381", {"start": v(-542.46, -62.2) * mm, "end": v(-542.46, -49.5) * mm});
            skLineSegment(sketch, "E382", {"start": v(-542.46, -73.63) * mm, "end": v(-542.46, -80.05) * mm});
            skLineSegment(sketch, "E383", {"start": v(-542.46, -62.2) * mm, "end": v(-518.33, -62.2) * mm});
            skLineSegment(sketch, "E384", {"start": v(-542.46, -80.05) * mm, "end": v(-466.26, -80.05) * mm});
            skPoint(sketch, "E385", {"position": v(-504.36, -80.05) * mm});
            skLineSegment(sketch, "E386", {"start": v(-542.46, 47.02) * mm, "end": v(-511.98, 47.02) * mm});
            skLineSegment(sketch, "E387", {"start": v(-511.98, 47.02) * mm, "end": v(-511.98, 64.8) * mm});
            skLineSegment(sketch, "E388", {"start": v(-511.98, 64.8) * mm, "end": v(-518.33, 64.8) * mm});
            skLineSegment(sketch, "E389", {"start": v(-518.33, 64.8) * mm, "end": v(-518.33, 58.45) * mm});
            skLineSegment(sketch, "E390", {"start": v(-518.33, 58.45) * mm, "end": v(-542.46, 58.45) * mm});
            skLineSegment(sketch, "E391", {"start": v(-542.46, 58.45) * mm, "end": v(-542.46, 71.15) * mm});
            skLineSegment(sketch, "E392", {"start": v(-542.46, 71.15) * mm, "end": v(-511.98, 71.15) * mm});
            skLineSegment(sketch, "E393", {"start": v(-511.98, 88.93) * mm, "end": v(-518.33, 88.93) * mm});
            skLineSegment(sketch, "E394", {"start": v(-518.33, 88.93) * mm, "end": v(-518.33, 82.58) * mm});
            skLineSegment(sketch, "E395", {"start": v(-518.33, 82.58) * mm, "end": v(-542.46, 82.58) * mm});
            skLineSegment(sketch, "E396", {"start": v(-542.46, 82.58) * mm, "end": v(-542.46, 95.28) * mm});
            skLineSegment(sketch, "E397", {"start": v(-466.26, 47.02) * mm, "end": v(-496.74, 47.02) * mm});
            skLineSegment(sketch, "E398", {"start": v(-496.74, 47.02) * mm, "end": v(-496.74, 64.8) * mm});
            skLineSegment(sketch, "E399", {"start": v(-496.74, 64.8) * mm, "end": v(-490.39, 64.8) * mm});
            skLineSegment(sketch, "E400", {"start": v(-490.39, 64.8) * mm, "end": v(-490.39, 58.45) * mm});
            skLineSegment(sketch, "E401", {"start": v(-490.39, 58.45) * mm, "end": v(-466.26, 58.45) * mm});
            skLineSegment(sketch, "E402", {"start": v(-466.26, 58.45) * mm, "end": v(-466.26, 71.15) * mm});
            skLineSegment(sketch, "E403", {"start": v(-466.26, 71.15) * mm, "end": v(-496.74, 71.15) * mm});
            skLineSegment(sketch, "E404", {"start": v(-496.74, 71.15) * mm, "end": v(-496.74, 88.93) * mm});
            skLineSegment(sketch, "E405", {"start": v(-496.74, 88.93) * mm, "end": v(-490.39, 88.93) * mm});
            skLineSegment(sketch, "E406", {"start": v(-490.39, 88.93) * mm, "end": v(-490.39, 82.58) * mm});
            skLineSegment(sketch, "E407", {"start": v(-490.39, 82.58) * mm, "end": v(-466.26, 82.58) * mm});
            skLineSegment(sketch, "E408", {"start": v(-466.26, 82.58) * mm, "end": v(-466.26, 95.28) * mm});
            skLineSegment(sketch, "E409", {"start": v(-511.98, 71.15) * mm, "end": v(-511.98, 88.93) * mm});
            skLineSegment(sketch, "E410", {"start": v(-542.46, 95.28) * mm, "end": v(-466.26, 95.28) * mm});
            skPoint(sketch, "E411", {"position": v(-504.36, 95.28) * mm});
            skLineSegment(sketch, "E412", {"start": v(-453.56, 47.02) * mm, "end": v(-423.08, 47.02) * mm});
            skLineSegment(sketch, "E413", {"start": v(-423.08, 47.02) * mm, "end": v(-423.08, 64.8) * mm});
            skLineSegment(sketch, "E414", {"start": v(-423.08, 64.8) * mm, "end": v(-429.43, 64.8) * mm});
            skLineSegment(sketch, "E415", {"start": v(-429.43, 64.8) * mm, "end": v(-429.43, 58.45) * mm});
            skLineSegment(sketch, "E416", {"start": v(-429.43, 58.45) * mm, "end": v(-453.56, 58.45) * mm});
            skLineSegment(sketch, "E417", {"start": v(-453.56, 58.45) * mm, "end": v(-453.56, 71.15) * mm});
            skLineSegment(sketch, "E418", {"start": v(-453.56, 71.15) * mm, "end": v(-423.08, 71.15) * mm});
            skLineSegment(sketch, "E419", {"start": v(-423.08, 88.93) * mm, "end": v(-429.43, 88.93) * mm});
            skLineSegment(sketch, "E420", {"start": v(-429.43, 88.93) * mm, "end": v(-429.43, 82.58) * mm});
            skLineSegment(sketch, "E421", {"start": v(-429.43, 82.58) * mm, "end": v(-453.56, 82.58) * mm});
            skLineSegment(sketch, "E422", {"start": v(-453.56, 82.58) * mm, "end": v(-453.56, 95.28) * mm});
            skLineSegment(sketch, "E423", {"start": v(-377.36, 47.02) * mm, "end": v(-407.84, 47.02) * mm});
            skLineSegment(sketch, "E424", {"start": v(-407.84, 47.02) * mm, "end": v(-407.84, 64.8) * mm});
            skLineSegment(sketch, "E425", {"start": v(-407.84, 64.8) * mm, "end": v(-401.49, 64.8) * mm});
            skLineSegment(sketch, "E426", {"start": v(-401.49, 64.8) * mm, "end": v(-401.49, 58.45) * mm});
            skLineSegment(sketch, "E427", {"start": v(-401.49, 58.45) * mm, "end": v(-377.36, 58.45) * mm});
            skLineSegment(sketch, "E428", {"start": v(-377.36, 58.45) * mm, "end": v(-377.36, 71.15) * mm});
            skLineSegment(sketch, "E429", {"start": v(-377.36, 71.15) * mm, "end": v(-407.84, 71.15) * mm});
            skLineSegment(sketch, "E430", {"start": v(-407.84, 71.15) * mm, "end": v(-407.84, 88.93) * mm});
            skLineSegment(sketch, "E431", {"start": v(-407.84, 88.93) * mm, "end": v(-401.49, 88.93) * mm});
            skLineSegment(sketch, "E432", {"start": v(-401.49, 88.93) * mm, "end": v(-401.49, 82.58) * mm});
            skLineSegment(sketch, "E433", {"start": v(-401.49, 82.58) * mm, "end": v(-377.36, 82.58) * mm});
            skLineSegment(sketch, "E434", {"start": v(-377.36, 82.58) * mm, "end": v(-377.36, 95.28) * mm});
            skLineSegment(sketch, "E435", {"start": v(-423.08, 71.15) * mm, "end": v(-423.08, 88.93) * mm});
            skLineSegment(sketch, "E436", {"start": v(-453.56, 95.28) * mm, "end": v(-377.36, 95.28) * mm});
            skPoint(sketch, "E437", {"position": v(-415.46, 95.28) * mm});
            skLineSegment(sketch, "E438", {"start": v(-364.66, 47.02) * mm, "end": v(-334.18, 47.02) * mm});
            skLineSegment(sketch, "E439", {"start": v(-334.18, 47.02) * mm, "end": v(-334.18, 64.8) * mm});
            skLineSegment(sketch, "E440", {"start": v(-334.18, 64.8) * mm, "end": v(-340.53, 64.8) * mm});
            skLineSegment(sketch, "E441", {"start": v(-340.53, 64.8) * mm, "end": v(-340.53, 58.45) * mm});
            skLineSegment(sketch, "E442", {"start": v(-340.53, 58.45) * mm, "end": v(-364.66, 58.45) * mm});
            skLineSegment(sketch, "E443", {"start": v(-364.66, 58.45) * mm, "end": v(-364.66, 71.15) * mm});
            skLineSegment(sketch, "E444", {"start": v(-364.66, 71.15) * mm, "end": v(-334.18, 71.15) * mm});
            skLineSegment(sketch, "E445", {"start": v(-334.18, 88.93) * mm, "end": v(-340.53, 88.93) * mm});
            skLineSegment(sketch, "E446", {"start": v(-340.53, 88.93) * mm, "end": v(-340.53, 82.58) * mm});
            skLineSegment(sketch, "E447", {"start": v(-340.53, 82.58) * mm, "end": v(-364.66, 82.58) * mm});
            skLineSegment(sketch, "E448", {"start": v(-364.66, 82.58) * mm, "end": v(-364.66, 95.28) * mm});
            skLineSegment(sketch, "E449", {"start": v(-288.46, 47.02) * mm, "end": v(-318.94, 47.02) * mm});
            skLineSegment(sketch, "E450", {"start": v(-318.94, 47.02) * mm, "end": v(-318.94, 64.8) * mm});
            skLineSegment(sketch, "E451", {"start": v(-318.94, 64.8) * mm, "end": v(-312.59, 64.8) * mm});
            skLineSegment(sketch, "E452", {"start": v(-312.59, 64.8) * mm, "end": v(-312.59, 58.45) * mm});
            skLineSegment(sketch, "E453", {"start": v(-312.59, 58.45) * mm, "end": v(-288.46, 58.45) * mm});
            skLineSegment(sketch, "E454", {"start": v(-288.46, 58.45) * mm, "end": v(-288.46, 71.15) * mm});
            skLineSegment(sketch, "E455", {"start": v(-288.46, 71.15) * mm, "end": v(-318.94, 71.15) * mm});
            skLineSegment(sketch, "E456", {"start": v(-318.94, 71.15) * mm, "end": v(-318.94, 88.93) * mm});
            skLineSegment(sketch, "E457", {"start": v(-318.94, 88.93) * mm, "end": v(-312.59, 88.93) * mm});
            skLineSegment(sketch, "E458", {"start": v(-312.59, 88.93) * mm, "end": v(-312.59, 82.58) * mm});
            skLineSegment(sketch, "E459", {"start": v(-312.59, 82.58) * mm, "end": v(-288.46, 82.58) * mm});
            skLineSegment(sketch, "E460", {"start": v(-288.46, 82.58) * mm, "end": v(-288.46, 95.28) * mm});
            skLineSegment(sketch, "E461", {"start": v(-334.18, 71.15) * mm, "end": v(-334.18, 88.93) * mm});
            skLineSegment(sketch, "E462", {"start": v(-364.66, 95.28) * mm, "end": v(-288.46, 95.28) * mm});
            skPoint(sketch, "E463", {"position": v(-326.56, 95.28) * mm});
            skLineSegment(sketch, "E464", {"start": v(-275.76, 47.02) * mm, "end": v(-245.28, 47.02) * mm});
            skLineSegment(sketch, "E465", {"start": v(-245.28, 47.02) * mm, "end": v(-245.28, 64.8) * mm});
            skLineSegment(sketch, "E466", {"start": v(-245.28, 64.8) * mm, "end": v(-251.63, 64.8) * mm});
            skLineSegment(sketch, "E467", {"start": v(-251.63, 64.8) * mm, "end": v(-251.63, 58.45) * mm});
            skLineSegment(sketch, "E468", {"start": v(-251.63, 58.45) * mm, "end": v(-275.76, 58.45) * mm});
            skLineSegment(sketch, "E469", {"start": v(-275.76, 58.45) * mm, "end": v(-275.76, 71.15) * mm});
            skLineSegment(sketch, "E470", {"start": v(-275.76, 71.15) * mm, "end": v(-245.28, 71.15) * mm});
            skLineSegment(sketch, "E471", {"start": v(-245.28, 88.93) * mm, "end": v(-251.63, 88.93) * mm});
            skLineSegment(sketch, "E472", {"start": v(-251.63, 88.93) * mm, "end": v(-251.63, 82.58) * mm});
            skLineSegment(sketch, "E473", {"start": v(-251.63, 82.58) * mm, "end": v(-275.76, 82.58) * mm});
            skLineSegment(sketch, "E474", {"start": v(-275.76, 82.58) * mm, "end": v(-275.76, 95.28) * mm});
            skLineSegment(sketch, "E475", {"start": v(-199.56, 47.02) * mm, "end": v(-230.04, 47.02) * mm});
            skLineSegment(sketch, "E476", {"start": v(-230.04, 47.02) * mm, "end": v(-230.04, 64.8) * mm});
            skLineSegment(sketch, "E477", {"start": v(-230.04, 64.8) * mm, "end": v(-223.69, 64.8) * mm});
            skLineSegment(sketch, "E478", {"start": v(-223.69, 64.8) * mm, "end": v(-223.69, 58.45) * mm});
            skLineSegment(sketch, "E479", {"start": v(-223.69, 58.45) * mm, "end": v(-199.56, 58.45) * mm});
            skLineSegment(sketch, "E480", {"start": v(-199.56, 58.45) * mm, "end": v(-199.56, 71.15) * mm});
            skLineSegment(sketch, "E481", {"start": v(-199.56, 71.15) * mm, "end": v(-230.04, 71.15) * mm});
            skLineSegment(sketch, "E482", {"start": v(-230.04, 71.15) * mm, "end": v(-230.04, 88.93) * mm});
            skLineSegment(sketch, "E483", {"start": v(-230.04, 88.93) * mm, "end": v(-223.69, 88.93) * mm});
            skLineSegment(sketch, "E484", {"start": v(-223.69, 88.93) * mm, "end": v(-223.69, 82.58) * mm});
            skLineSegment(sketch, "E485", {"start": v(-223.69, 82.58) * mm, "end": v(-199.56, 82.58) * mm});
            skLineSegment(sketch, "E486", {"start": v(-199.56, 82.58) * mm, "end": v(-199.56, 95.28) * mm});
            skLineSegment(sketch, "E487", {"start": v(-245.28, 71.15) * mm, "end": v(-245.28, 88.93) * mm});
            skLineSegment(sketch, "E488", {"start": v(-275.76, 95.28) * mm, "end": v(-199.56, 95.28) * mm});
            skPoint(sketch, "E489", {"position": v(-237.66, 95.28) * mm});
            skLineSegment(sketch, "E490", {"start": v(-186.86, 47.02) * mm, "end": v(-156.38, 47.02) * mm});
            skLineSegment(sketch, "E491", {"start": v(-156.38, 47.02) * mm, "end": v(-156.38, 64.8) * mm});
            skLineSegment(sketch, "E492", {"start": v(-156.38, 64.8) * mm, "end": v(-162.73, 64.8) * mm});
            skLineSegment(sketch, "E493", {"start": v(-162.73, 64.8) * mm, "end": v(-162.73, 58.45) * mm});
            skLineSegment(sketch, "E494", {"start": v(-162.73, 58.45) * mm, "end": v(-186.86, 58.45) * mm});
            skLineSegment(sketch, "E495", {"start": v(-186.86, 58.45) * mm, "end": v(-186.86, 71.15) * mm});
            skLineSegment(sketch, "E496", {"start": v(-186.86, 71.15) * mm, "end": v(-156.38, 71.15) * mm});
            skLineSegment(sketch, "E497", {"start": v(-156.38, 88.93) * mm, "end": v(-162.73, 88.93) * mm});
            skLineSegment(sketch, "E498", {"start": v(-162.73, 88.93) * mm, "end": v(-162.73, 82.58) * mm});
            skLineSegment(sketch, "E499", {"start": v(-162.73, 82.58) * mm, "end": v(-186.86, 82.58) * mm});
            skLineSegment(sketch, "E500", {"start": v(-186.86, 82.58) * mm, "end": v(-186.86, 95.28) * mm});
            skLineSegment(sketch, "E501", {"start": v(-110.66, 47.02) * mm, "end": v(-141.14, 47.02) * mm});
            skLineSegment(sketch, "E502", {"start": v(-141.14, 47.02) * mm, "end": v(-141.14, 64.8) * mm});
            skLineSegment(sketch, "E503", {"start": v(-141.14, 64.8) * mm, "end": v(-134.79, 64.8) * mm});
            skLineSegment(sketch, "E504", {"start": v(-134.79, 64.8) * mm, "end": v(-134.79, 58.45) * mm});
            skLineSegment(sketch, "E505", {"start": v(-134.79, 58.45) * mm, "end": v(-110.66, 58.45) * mm});
            skLineSegment(sketch, "E506", {"start": v(-110.66, 58.45) * mm, "end": v(-110.66, 71.15) * mm});
            skLineSegment(sketch, "E507", {"start": v(-110.66, 71.15) * mm, "end": v(-141.14, 71.15) * mm});
            skLineSegment(sketch, "E508", {"start": v(-141.14, 71.15) * mm, "end": v(-141.14, 88.93) * mm});
            skLineSegment(sketch, "E509", {"start": v(-141.14, 88.93) * mm, "end": v(-134.79, 88.93) * mm});
            skLineSegment(sketch, "E510", {"start": v(-134.79, 88.93) * mm, "end": v(-134.79, 82.58) * mm});
            skLineSegment(sketch, "E511", {"start": v(-134.79, 82.58) * mm, "end": v(-110.66, 82.58) * mm});
            skLineSegment(sketch, "E512", {"start": v(-110.66, 82.58) * mm, "end": v(-110.66, 95.28) * mm});
            skLineSegment(sketch, "E513", {"start": v(-156.38, 71.15) * mm, "end": v(-156.38, 88.93) * mm});
            skLineSegment(sketch, "E514", {"start": v(-186.86, 95.28) * mm, "end": v(-110.66, 95.28) * mm});
            skPoint(sketch, "E515", {"position": v(-148.76, 95.28) * mm});
            skLineSegment(sketch, "E516", {"start": v(-97.96, 47.02) * mm, "end": v(-67.48, 47.02) * mm});
            skLineSegment(sketch, "E517", {"start": v(-67.48, 47.02) * mm, "end": v(-67.48, 64.8) * mm});
            skLineSegment(sketch, "E518", {"start": v(-67.48, 64.8) * mm, "end": v(-73.83, 64.8) * mm});
            skLineSegment(sketch, "E519", {"start": v(-73.83, 64.8) * mm, "end": v(-73.83, 58.45) * mm});
            skLineSegment(sketch, "E520", {"start": v(-73.83, 58.45) * mm, "end": v(-97.96, 58.45) * mm});
            skLineSegment(sketch, "E521", {"start": v(-97.96, 58.45) * mm, "end": v(-97.96, 71.15) * mm});
            skLineSegment(sketch, "E522", {"start": v(-97.96, 71.15) * mm, "end": v(-67.48, 71.15) * mm});
            skLineSegment(sketch, "E523", {"start": v(-67.48, 88.93) * mm, "end": v(-73.83, 88.93) * mm});
            skLineSegment(sketch, "E524", {"start": v(-73.83, 88.93) * mm, "end": v(-73.83, 82.58) * mm});
            skLineSegment(sketch, "E525", {"start": v(-73.83, 82.58) * mm, "end": v(-97.96, 82.58) * mm});
            skLineSegment(sketch, "E526", {"start": v(-97.96, 82.58) * mm, "end": v(-97.96, 95.28) * mm});
            skLineSegment(sketch, "E527", {"start": v(-21.76, 47.02) * mm, "end": v(-52.24, 47.02) * mm});
            skLineSegment(sketch, "E528", {"start": v(-52.24, 47.02) * mm, "end": v(-52.24, 64.8) * mm});
            skLineSegment(sketch, "E529", {"start": v(-52.24, 64.8) * mm, "end": v(-45.89, 64.8) * mm});
            skLineSegment(sketch, "E530", {"start": v(-45.89, 64.8) * mm, "end": v(-45.89, 58.45) * mm});
            skLineSegment(sketch, "E531", {"start": v(-45.89, 58.45) * mm, "end": v(-21.76, 58.45) * mm});
            skLineSegment(sketch, "E532", {"start": v(-21.76, 58.45) * mm, "end": v(-21.76, 71.15) * mm});
            skLineSegment(sketch, "E533", {"start": v(-21.76, 71.15) * mm, "end": v(-52.24, 71.15) * mm});
            skLineSegment(sketch, "E534", {"start": v(-52.24, 71.15) * mm, "end": v(-52.24, 88.93) * mm});
            skLineSegment(sketch, "E535", {"start": v(-52.24, 88.93) * mm, "end": v(-45.89, 88.93) * mm});
            skLineSegment(sketch, "E536", {"start": v(-45.89, 88.93) * mm, "end": v(-45.89, 82.58) * mm});
            skLineSegment(sketch, "E537", {"start": v(-45.89, 82.58) * mm, "end": v(-21.76, 82.58) * mm});
            skLineSegment(sketch, "E538", {"start": v(-21.76, 82.58) * mm, "end": v(-21.76, 95.28) * mm});
            skLineSegment(sketch, "E539", {"start": v(-67.48, 71.15) * mm, "end": v(-67.48, 88.93) * mm});
            skLineSegment(sketch, "E540", {"start": v(-97.96, 95.28) * mm, "end": v(-21.76, 95.28) * mm});
            skPoint(sketch, "E541", {"position": v(-59.86, 95.28) * mm});
            skLineSegment(sketch, "E542", {"start": v(-288.46, 95.28) * mm, "end": v(-275.76, 95.28) * mm});
            skPoint(sketch, "E543", {"position": v(-282.1, 95.28) * mm});
            skSolve(sketch);
        }
        {
            var Q0;
            Q0=makeQuery(id+"F0.imprint","IMPRINT",FACE,{"disambiguationData":[TD([[makeQuery(id+"F0.imprint","IMPRINT",EDGE,{"derivedFrom":sQuery(id+"F0.wireOp",EDGE,"E0")}),1.0]])]});
            extrude(context, id + "F1", {"entities" : qUnion([Q0]), "depth" : 6.35 * mm});
        }
    });
